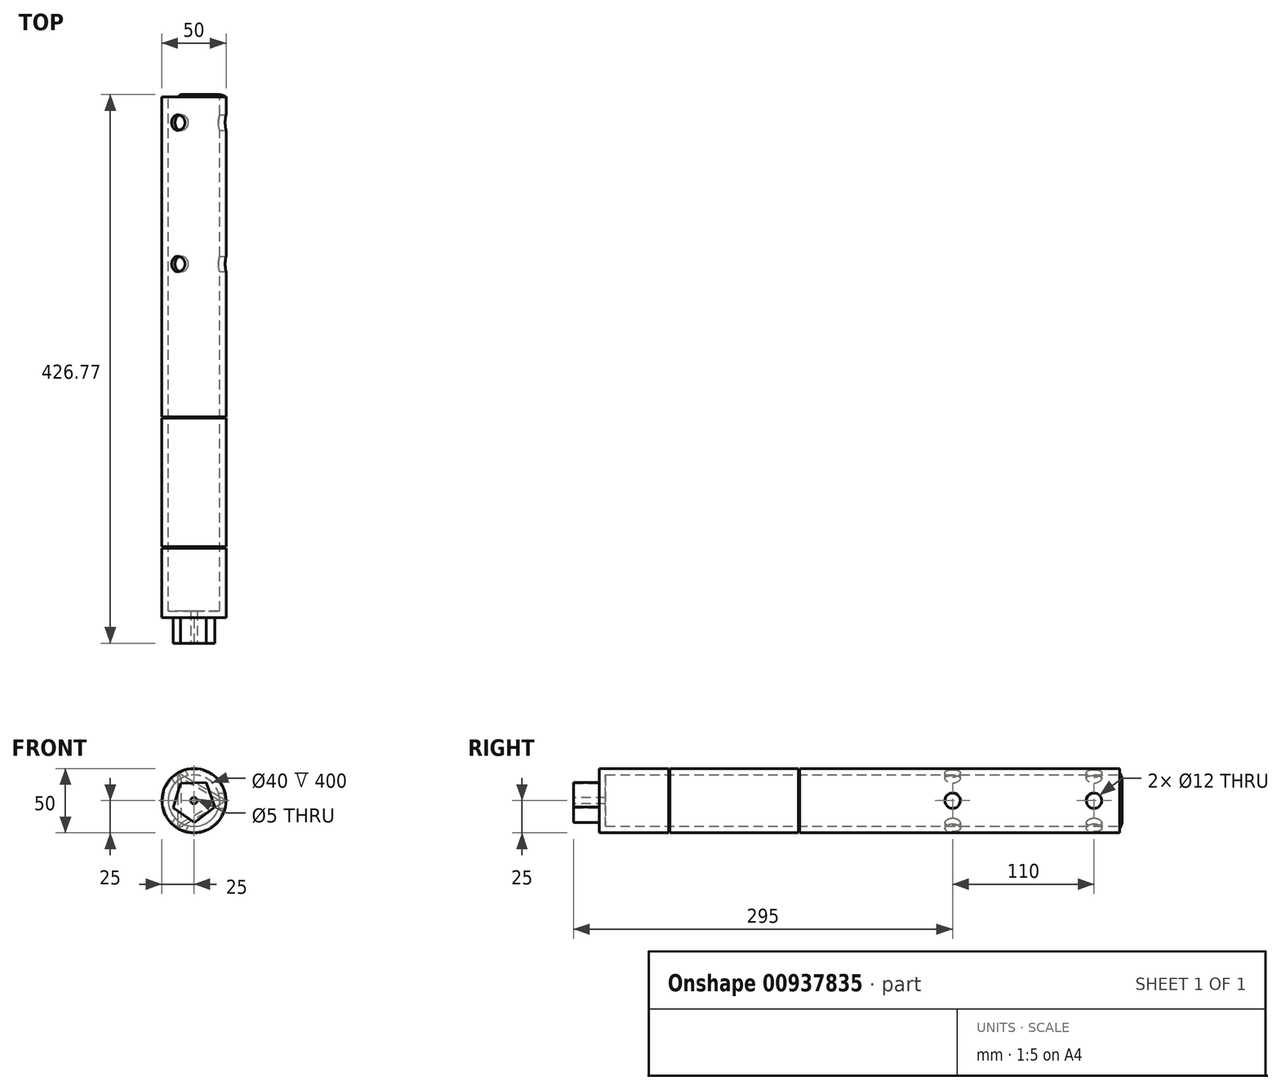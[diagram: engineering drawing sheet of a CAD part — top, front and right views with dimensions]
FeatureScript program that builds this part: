
annotation { "Feature Type Name" : "Feature", "Feature Type Description" : "" }
export const myFeature = defineFeature(function(context is Context, id is Id, definition is map)
    precondition{}
    {
        {
            var Q0;
            Q0=qCreatedBy(makeId("Front.planeOp"),FACE);
            var sketch = newSketch(context, id + "F0", { "sketchPlane" : qUnion([Q0])});
            skCircle(sketch, "E0", {"center": v(0, 0) * mm, "radius": 25 * mm});
            skCircle(sketch, "E1", {"center": v(0, 0) * mm, "radius": 20 * mm});
            skSolve(sketch);
        }
        {
            var Q0;
            Q0=makeQuery(id+"F0.imprint","IMPRINT",FACE,{"disambiguationData":[TD([[makeQuery(id+"F0.imprint","IMPRINT",EDGE,{"derivedFrom":sQuery(id+"F0.wireOp",EDGE,"E0")}),1.0]])]});
            extrude(context, id + "F1", {"entities" : qUnion([Q0]), "depth" : 400 * mm, "offsetDistance" : 25 * mm});
        }
        {
            var Q0;
            Q0=makeQuery(id+"F1.opExtrude","CAP_FACE",FACE,{"disambiguationData":[OSD([sQuery(id+"F0.wireOp",EDGE,"E0"),sQuery(id+"F0.wireOp",EDGE,"E1")])],"isStart":false});
            var sketch = newSketch(context, id + "F2", { "sketchPlane" : qUnion([Q0])});
            skCircle(sketch, "E2", {"center": v(0, 0) * mm, "radius": 25 * mm});
            skSolve(sketch);
        }
        {
            var Q0;
            Q0=qSketchRegion(id+"F2",true);
            extrude(context, id + "F3", {"entities" : qUnion([Q0]), "operationType" : NewBodyOperationType.ADD, "depth" : 5 * mm, "offsetDistance" : 25 * mm});
        }
        {
            var Q0;
            Q0=makeQuery(id+"F3.opExtrude","CAP_FACE",FACE,{"disambiguationData":[OSD([sQuery(id+"F2.wireOp",EDGE,"E2")])],"isStart":false});
            var sketch = newSketch(context, id + "F4", { "sketchPlane" : qUnion([Q0])});
            skCircle(sketch, "E3.cCircle", {"center": v(0, 0) * mm, "radius": 13.77 * mm, "construction": true});
            skLineSegment(sketch, "E3.0", {"start": v(0.38, -17.01) * mm, "end": v(-16.06, -5.62) * mm});
            skLineSegment(sketch, "E3.1", {"start": v(-16.06, -5.62) * mm, "end": v(-10.3, 13.54) * mm});
            skLineSegment(sketch, "E3.2", {"start": v(-10.3, 13.54) * mm, "end": v(9.7, 13.99) * mm});
            skLineSegment(sketch, "E3.3", {"start": v(9.7, 13.99) * mm, "end": v(16.3, -4.9) * mm});
            skLineSegment(sketch, "E3.4", {"start": v(16.3, -4.9) * mm, "end": v(0.38, -17.01) * mm});
            skPoint(sketch, "E3.0.midPoint", {"position": v(-7.84, -11.32) * mm});
            skSolve(sketch);
        }
        {
            var Q0;
            Q0=makeQuery(id+"F4.imprint","IMPRINT",FACE,{"disambiguationData":[TD([[makeQuery(id+"F4.imprint","IMPRINT",EDGE,{"derivedFrom":sQuery(id+"F4.wireOp",EDGE,"E3.0")}),-1.0]])]});
            extrude(context, id + "F5", {"entities" : qUnion([Q0]), "operationType" : NewBodyOperationType.ADD, "depth" : 20 * mm, "offsetDistance" : 25 * mm});
        }
        {
            var Q0;
            Q0=makeQuery(id+"F5.opExtrude","CAP_FACE",FACE,{"disambiguationData":[OSD([sQuery(id+"F4.wireOp",EDGE,"E3.0"),sQuery(id+"F4.wireOp",EDGE,"E3.1"),sQuery(id+"F4.wireOp",EDGE,"E3.2"),sQuery(id+"F4.wireOp",EDGE,"E3.3"),sQuery(id+"F4.wireOp",EDGE,"E3.4")])],"isStart":false});
            var sketch = newSketch(context, id + "F6", { "sketchPlane" : qUnion([Q0])});
            skPoint(sketch, "E4", {"position": v(0, 0) * mm});
            skSolve(sketch);
        }
        {
            var Q0;
            Q0=sQuery(id+"F6.wireOp",VERTEX,"E4");
            var Q1;
            Q1=makeQuery(id+"F1.opExtrude","SWEPT_BODY",BODY,{"disambiguationData":[OSD([sQuery(id+"F0.wireOp",EDGE,"E0"),sQuery(id+"F0.wireOp",EDGE,"E1")])]});
            hole(context, id + "F7", {"style" : HoleStyle.SIMPLE, "endStyle" : HoleEndStyle.THROUGH, "holeDiameter" : 5 * mm, "majorDiameter" : 5 * mm, "isTappedThrough" : true, "tappedDepth" : 12 * mm, "tapClearance" : 3, "locations" : qUnion([Q0]), "scope" : qUnion([Q1])});
        }
        {
            var Q0;
            Q0=qCreatedBy(makeId("Right.planeOp"),FACE);
            cPlane(context, id + "F8", {"entities" : qUnion([Q0]), "cplaneType" : CPlaneType.OFFSET, "offset" : 25 * mm, "width" : 150 * mm, "height" : 150 * mm});
        }
        {
            var Q0;
            Q0=qCreatedBy(id+"F8.planeOp",FACE);
            var sketch = newSketch(context, id + "F9", { "sketchPlane" : qUnion([Q0])});
            skPoint(sketch, "E5", {"position": v(-20, 0) * mm});
            skPoint(sketch, "E6", {"position": v(-130, 0) * mm});
            skSolve(sketch);
        }
        {
            var Q0;
            Q0=sQuery(id+"F9.wireOp",VERTEX,"E5");
            var Q1;
            Q1=sQuery(id+"F9.wireOp",VERTEX,"E6");
            var Q2;
            Q2=makeQuery(id+"F1.opExtrude","SWEPT_BODY",BODY,{"disambiguationData":[OSD([sQuery(id+"F0.wireOp",EDGE,"E0"),sQuery(id+"F0.wireOp",EDGE,"E1")])]});
            hole(context, id + "F10", {"style" : HoleStyle.SIMPLE, "endStyle" : HoleEndStyle.BLIND, "holeDiameter" : 12 * mm, "majorDiameter" : 5 * mm, "holeDepth" : 6 * mm, "isTappedThrough" : true, "tappedDepth" : 12 * mm, "tapClearance" : 3, "locations" : qUnion([Q0, Q1]), "scope" : qUnion([Q2])});
        }
        {
            var Q0;
            Q0=makeQuery(id+"F1.opExtrude","CAP_FACE",FACE,{"disambiguationData":[OSD([sQuery(id+"F0.wireOp",EDGE,"E0"),sQuery(id+"F0.wireOp",EDGE,"E1")])],"isStart":true});
            var sketch = newSketch(context, id + "F11", { "sketchPlane" : qUnion([Q0])});
            skCircle(sketch, "E7.cCircle", {"center": v(0, 0) * mm, "radius": 12.5 * mm, "construction": true});
            skLineSegment(sketch, "E7.0", {"start": v(12.5, 21.65) * mm, "end": v(12.5, -21.65) * mm});
            skLineSegment(sketch, "E7.1", {"start": v(12.5, -21.65) * mm, "end": v(-25, 0) * mm});
            skLineSegment(sketch, "E7.2", {"start": v(-25, 0) * mm, "end": v(12.5, 21.65) * mm});
            skPoint(sketch, "E7.0.midPoint", {"position": v(12.5, 0) * mm});
            skSolve(sketch);
        }
        {
            var Q0;
            Q0=qSketchRegion(id+"F11",true);
            extrude(context, id + "F12", {"entities" : qUnion([Q0]), "operationType" : NewBodyOperationType.ADD, "depth" : 2 * mm, "offsetDistance" : 25 * mm});
        }
        {
            var Q0;
            Q0=qCreatedBy(makeId("Front.planeOp"),FACE);
            cPlane(context, id + "F13", {"entities" : qUnion([Q0]), "cplaneType" : CPlaneType.OFFSET, "offset" : 25 * mm, "width" : 150 * mm, "height" : 150 * mm});
        }
        {
            var Q0;
            Q0=makeQuery(id+"F12.opExtrude","SWEPT_FACE",FACE,{"disambiguationData":[OSD([sQuery(id+"F11.wireOp",EDGE,"E7.2")])]});
            cPlane(context, id + "F14", {"entities" : qUnion([Q0]), "cplaneType" : CPlaneType.OFFSET, "offset" : 37.5 * mm, "oppositeDirection" : true, "width" : 150 * mm, "height" : 150 * mm});
        }
        {
            var Q0;
            Q0=makeQuery(id+"F12.opExtrude","SWEPT_FACE",FACE,{"disambiguationData":[OSD([sQuery(id+"F11.wireOp",EDGE,"E7.1")])]});
            cPlane(context, id + "F15", {"entities" : qUnion([Q0]), "cplaneType" : CPlaneType.OFFSET, "offset" : 37.5 * mm, "oppositeDirection" : true, "width" : 150 * mm, "height" : 150 * mm});
        }
        {
            var Q0;
            Q0=qCreatedBy(id+"F14.planeOp",FACE);
            var sketch = newSketch(context, id + "F16", { "sketchPlane" : qUnion([Q0])});
            skLineSegment(sketch, "E8", {"start": v(0, 0) * mm, "end": v(0, -597.57) * mm});
            skPoint(sketch, "E9", {"position": v(0, -20) * mm});
            skPoint(sketch, "E10", {"position": v(0, -130) * mm});
            skSolve(sketch);
        }
        {
            var Q0;
            Q0=sQuery(id+"F16.wireOp",VERTEX,"E9");
            var Q1;
            Q1=sQuery(id+"F16.wireOp",VERTEX,"E10");
            var Q2;
            Q2=makeQuery(id+"F1.opExtrude","SWEPT_BODY",BODY,{"disambiguationData":[OSD([sQuery(id+"F0.wireOp",EDGE,"E0"),sQuery(id+"F0.wireOp",EDGE,"E1")])]});
            hole(context, id + "F17", {"style" : HoleStyle.SIMPLE, "endStyle" : HoleEndStyle.BLIND, "oppositeDirection" : true, "holeDiameter" : 12 * mm, "majorDiameter" : 5 * mm, "holeDepth" : 6 * mm, "isTappedThrough" : true, "tappedDepth" : 12 * mm, "tapClearance" : 3, "locations" : qUnion([Q0, Q1]), "scope" : qUnion([Q2])});
        }
        {
            var Q0;
            Q0=qCreatedBy(id+"F15.planeOp",FACE);
            var sketch = newSketch(context, id + "F18", { "sketchPlane" : qUnion([Q0])});
            skLineSegment(sketch, "E11", {"start": v(0, 0) * mm, "end": v(0, 1140.88) * mm});
            skPoint(sketch, "E12", {"position": v(0, 20) * mm});
            skPoint(sketch, "E13", {"position": v(0, 130) * mm});
            skSolve(sketch);
        }
        {
            var Q0;
            Q0=sQuery(id+"F18.wireOp",VERTEX,"E12");
            var Q1;
            Q1=sQuery(id+"F18.wireOp",VERTEX,"E13");
            var Q2;
            Q2=makeQuery(id+"F1.opExtrude","SWEPT_BODY",BODY,{"disambiguationData":[OSD([sQuery(id+"F0.wireOp",EDGE,"E0"),sQuery(id+"F0.wireOp",EDGE,"E1")])]});
            hole(context, id + "F19", {"style" : HoleStyle.SIMPLE, "endStyle" : HoleEndStyle.BLIND, "oppositeDirection" : true, "holeDiameter" : 12 * mm, "majorDiameter" : 5 * mm, "holeDepth" : 6 * mm, "isTappedThrough" : true, "tappedDepth" : 12 * mm, "tapClearance" : 3, "locations" : qUnion([Q0, Q1]), "scope" : qUnion([Q2])});
        }
        {
            var Q0;
            Q0=qCreatedBy(makeId("Front.planeOp"),FACE);
            cPlane(context, id + "F20", {"entities" : qUnion([Q0]), "cplaneType" : CPlaneType.OFFSET, "offset" : 250 * mm, "width" : 150 * mm, "height" : 150 * mm});
        }
        {
            var Q0;
            Q0=qCreatedBy(id+"F20.planeOp",FACE);
            var sketch = newSketch(context, id + "F21", { "sketchPlane" : qUnion([Q0])});
            skCircle(sketch, "E14", {"center": v(0, 0) * mm, "radius": 24 * mm});
            skCircle(sketch, "E15", {"center": v(0, 0) * mm, "radius": 25 * mm});
            skSolve(sketch);
        }
        {
            var Q0;
            Q0=qSketchRegion(id+"F21",true);
            extrude(context, id + "F22", {"entities" : qUnion([Q0]), "operationType" : NewBodyOperationType.REMOVE, "oppositeDirection" : true, "depth" : 1 * mm, "offsetDistance" : 25 * mm});
        }
        {
            var Q0;
            Q0=qCreatedBy(id+"F20.planeOp",FACE);
            cPlane(context, id + "F23", {"entities" : qUnion([Q0]), "cplaneType" : CPlaneType.OFFSET, "offset" : 100 * mm, "width" : 150 * mm, "height" : 150 * mm});
        }
        {
            var Q0;
            Q0=qCreatedBy(id+"F23.planeOp",FACE);
            var sketch = newSketch(context, id + "F24", { "sketchPlane" : qUnion([Q0])});
            skCircle(sketch, "E16", {"center": v(0, 0) * mm, "radius": 24 * mm});
            skCircle(sketch, "E17", {"center": v(0, 0) * mm, "radius": 25 * mm});
            skSolve(sketch);
        }
        {
            var Q0;
            Q0=qSketchRegion(id+"F24",true);
            extrude(context, id + "F25", {"entities" : qUnion([Q0]), "operationType" : NewBodyOperationType.REMOVE, "depth" : 1 * mm, "offsetDistance" : 25 * mm});
        }
        {
            var Q0;
            Q0=makeQuery(id+"F12.opExtrude","CAP_FACE",FACE,{"disambiguationData":[OSD([sQuery(id+"F11.wireOp",EDGE,"E7.0"),sQuery(id+"F11.wireOp",EDGE,"E7.1"),sQuery(id+"F11.wireOp",EDGE,"E7.2")])],"isStart":false});
            var sketch = newSketch(context, id + "F26", { "sketchPlane" : qUnion([Q0])});
            skCircle(sketch, "E18.cCircle", {"center": v(0, 0) * mm, "radius": 10 * mm, "construction": true});
            skLineSegment(sketch, "E18.0", {"start": v(10, -17.32) * mm, "end": v(-20, 0) * mm});
            skLineSegment(sketch, "E18.1", {"start": v(-20, 0) * mm, "end": v(10, 17.32) * mm});
            skLineSegment(sketch, "E18.2", {"start": v(10, 17.32) * mm, "end": v(10, -17.32) * mm});
            skPoint(sketch, "E18.0.midPoint", {"position": v(-5, -8.66) * mm});
            skSolve(sketch);
        }
        {
            var Q0;
            Q0=makeQuery(id+"F26.imprint","IMPRINT",FACE,{"disambiguationData":[TD([[makeQuery(id+"F26.imprint","IMPRINT",EDGE,{"derivedFrom":sQuery(id+"F26.wireOp",EDGE,"E18.0")}),-1.0]])]});
            extrude(context, id + "F27", {"entities" : qUnion([Q0]), "operationType" : NewBodyOperationType.REMOVE, "oppositeDirection" : true, "depth" : 20 * mm, "offsetDistance" : 25 * mm});
        }
        {
            var Q0;
            Q0=makeQuery(id+"F12.opExtrude","CAP_EDGE",EDGE,{"disambiguationData":[OSD([sQuery(id+"F11.wireOp",EDGE,"E7.1")])],"isStart":false});
            var Q1;
            Q1=makeQuery(id+"F12.opExtrude","CAP_EDGE",EDGE,{"disambiguationData":[OSD([sQuery(id+"F11.wireOp",EDGE,"E7.0")])],"isStart":false});
            var Q2;
            Q2=makeQuery(id+"F12.opExtrude","CAP_EDGE",EDGE,{"disambiguationData":[OSD([sQuery(id+"F11.wireOp",EDGE,"E7.2")])],"isStart":false});
            fillet(context, id + "F28", {"entities" : qUnion([Q0, Q1, Q2]), "radius" : 5 * mm, "tangentPropagation" : true, "allowEdgeOverflow" : false});
        }
    });
